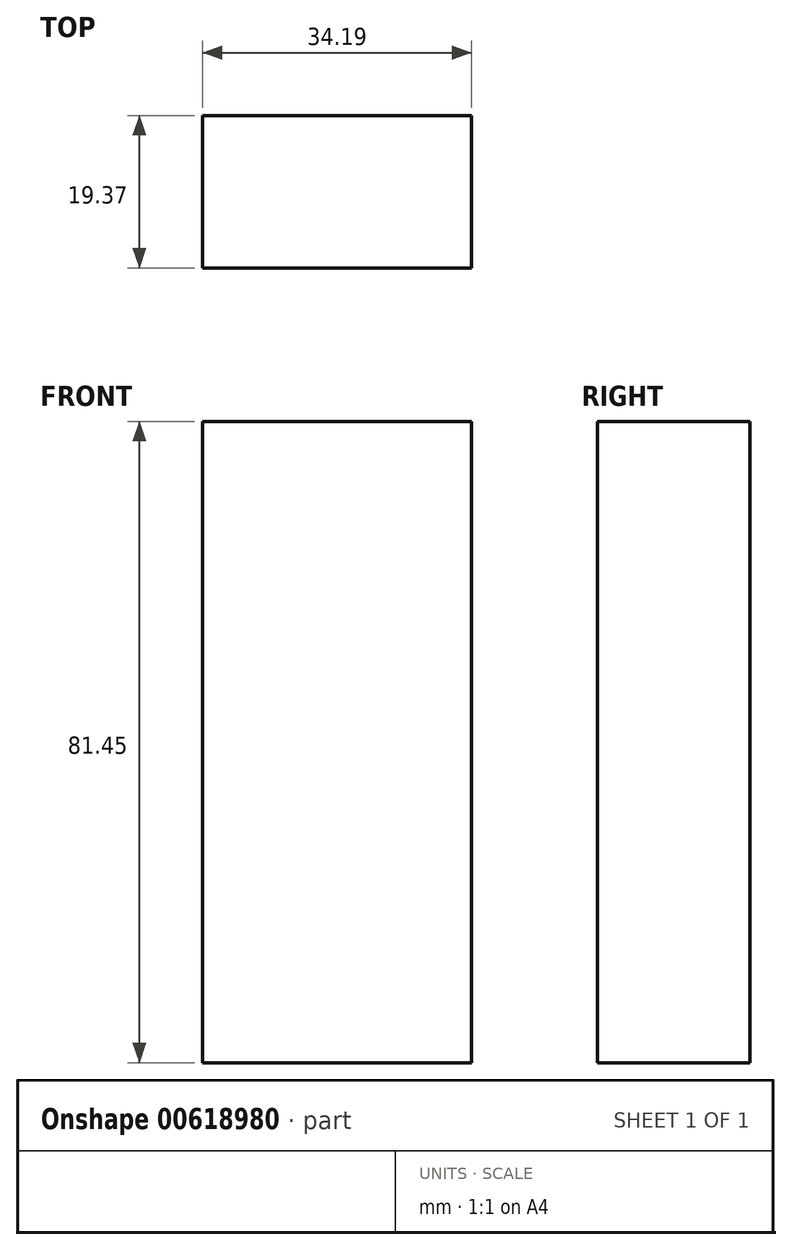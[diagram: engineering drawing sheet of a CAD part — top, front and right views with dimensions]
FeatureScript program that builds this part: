
annotation { "Feature Type Name" : "Feature", "Feature Type Description" : "" }
export const myFeature = defineFeature(function(context is Context, id is Id, definition is map)
    precondition{}
    {
        {
            var Q0;
            Q0=qCreatedBy(makeId("Top.planeOp"),FACE);
            var sketch = newSketch(context, id + "F0", { "sketchPlane" : qUnion([Q0])});
            skLineSegment(sketch, "E0.bottom", {"start": v(0, 19.37) * mm, "end": v(34.19, 19.37) * mm});
            skLineSegment(sketch, "E0.top", {"start": v(0, 0) * mm, "end": v(34.19, 0) * mm});
            skLineSegment(sketch, "E0.left", {"start": v(0, 19.37) * mm, "end": v(0, 0) * mm});
            skLineSegment(sketch, "E0.right", {"start": v(34.19, 19.37) * mm, "end": v(34.19, 0) * mm});
            skSolve(sketch);
        }
        {
            var Q0;
            Q0 = qSketchRegion(id + "F0", true);
            extrude(context, id + "F1", {"entities" : qUnion([Q0]), "depth" : 81.45 * mm, "offsetDistance" : 25.4 * mm});
        }
    });
